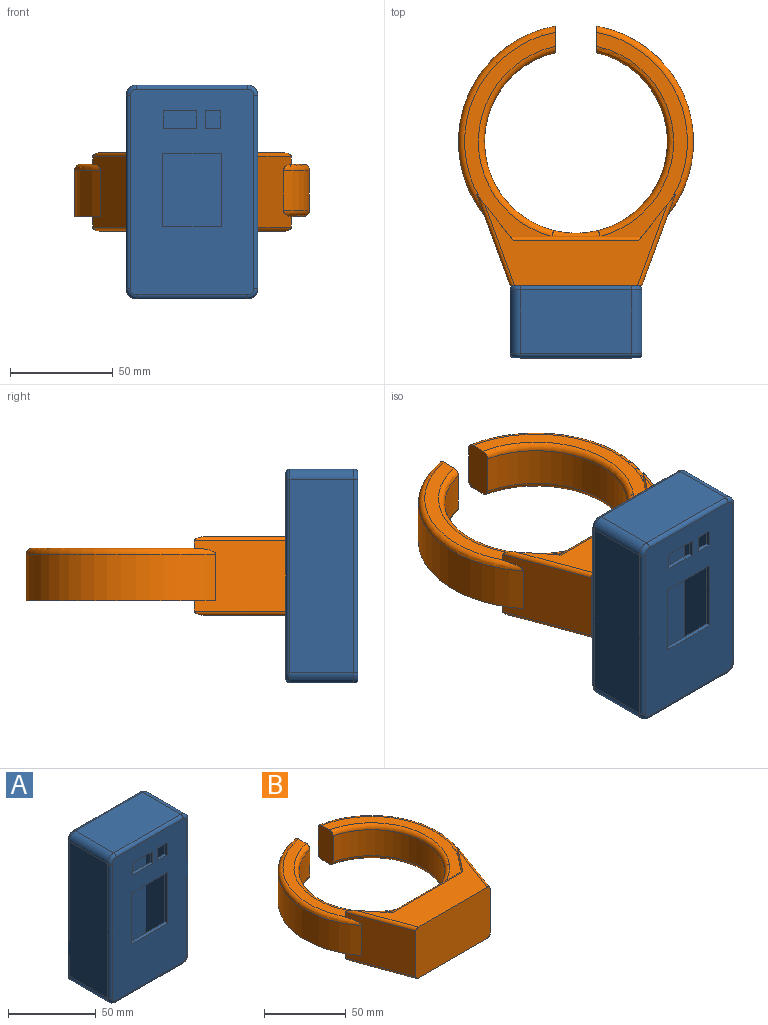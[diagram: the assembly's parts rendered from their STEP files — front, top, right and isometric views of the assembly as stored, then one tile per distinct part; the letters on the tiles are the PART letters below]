
ASSEMBLY  parts=2 mates=1
PART A: 44 faces, bbox 64.8x35x104.8 mm
  f0: plane 100x60mm, normal (0,-1,0), area 4771.6mm2, adj f11,f12,f13,f14,f15,f16,f17,f18
  f1: plane 100x60mm, normal (0,1,0), area 4779.3mm2, adj f27,f28,f29,f30,f31,f32,f33,f34
  f2: plane 54x31mm, normal (0,0,1), area 1674mm2, adj f9,f10,f11,f19
  f3: plane 94x31mm, normal (1,0,0), area 2914mm2, adj f8,f9,f14,f22
  f4: plane 94x31mm, normal (-1,0,0), area 2914mm2, adj f7,f10,f15,f23
  f5: plane 100x60mm, normal (0,1,0), area 5992.3mm2, adj f19,f20,f21,f22,f23,f24,f25,f26
  f6: plane 54x31mm, normal (0,0,-1), area 1674mm2, adj f7,f8,f18,f26
  f7: cylinder r=5mm len=31mm, axis (0,1,0), area 243.5mm2, adj f4,f6,f17,f25
  f8: cylinder r=5mm len=31mm, axis (0,-1,0), area 243.5mm2, adj f3,f6,f16,f24
  f9: cylinder r=5mm len=31mm, axis (0,-1,0), area 243.5mm2, adj f2,f3,f12,f20
  f10: cylinder r=5mm len=31mm, axis (0,1,0), area 243.5mm2, adj f2,f4,f13,f21
  f11: cylinder r=2mm len=54mm, axis (-1,0,0), area 169.6mm2, adj f0,f2,f12,f13
  f12: torus R=3mm, axis (0,-1,0), area 21.1mm2, adj f0,f9,f11,f14
  f13: torus R=3mm, axis (0,-1,0), area 21.1mm2, adj f0,f10,f11,f15
  f14: cylinder r=2mm len=94mm, axis (0,0,1), area 295.3mm2, adj f0,f3,f12,f16
  f15: cylinder r=2mm len=94mm, axis (0,0,-1), area 295.3mm2, adj f0,f4,f13,f17
  f16: torus R=3mm, axis (0,-1,0), area 21.1mm2, adj f0,f8,f14,f18
  f17: torus R=3mm, axis (0,-1,0), area 21.1mm2, adj f0,f7,f15,f18
  f18: cylinder r=2mm len=54mm, axis (-1,0,0), area 169.6mm2, adj f0,f6,f16,f17
  f19: cylinder r=2mm len=54mm, axis (1,0,0), area 169.6mm2, adj f2,f5,f20,f21
  f20: torus R=3mm, axis (0,-1,0), area 21.1mm2, adj f5,f9,f19,f22
  f21: torus R=3mm, axis (0,-1,0), area 21.1mm2, adj f5,f10,f19,f23
  f22: cylinder r=2mm len=94mm, axis (0,0,-1), area 295.3mm2, adj f3,f5,f20,f24
  f23: cylinder r=2mm len=94mm, axis (0,0,1), area 295.3mm2, adj f4,f5,f21,f25
  f24: torus R=3mm, axis (0,-1,0), area 21.1mm2, adj f5,f8,f22,f26
  f25: torus R=3mm, axis (0,-1,0), area 21.1mm2, adj f5,f7,f23,f26
  f26: cylinder r=2mm len=54mm, axis (1,0,0), area 169.6mm2, adj f5,f6,f24,f25
  f27: plane 7.5x2mm, normal (0,0,-1), area 15mm2, adj f0,f1,f28,f30
  f28: plane 8.4x2mm, normal (1,0,0), area 16.8mm2, adj f0,f1,f27,f29
  f29: plane 7.5x2mm, normal (0,0,1), area 15mm2, adj f0,f1,f28,f30
  f30: plane 8.4x2mm, normal (-1,0,0), area 16.8mm2, adj f0,f1,f27,f29
  f31: plane 16.3x2mm, normal (0,0,-1), area 32.6mm2, adj f0,f1,f32,f34
  f32: plane 8.4x2mm, normal (1,0,0), area 16.8mm2, adj f0,f1,f31,f33
  f33: plane 16.3x2mm, normal (0,0,1), area 32.6mm2, adj f0,f1,f32,f34
  f34: plane 8.4x2mm, normal (-1,0,0), area 16.8mm2, adj f0,f1,f31,f33
  f35: plane 60x31mm, normal (0,0,1), area 1860mm2, adj f1,f37,f38,f39
  f36: plane 60x31mm, normal (0,0,-1), area 1860mm2, adj f1,f37,f38,f39
  f37: plane 100x31mm, normal (1,0,0), area 3100mm2, adj f1,f35,f36,f38
  f38: plane 100x60mm, normal (0,-1,0), area 6000mm2, adj f35,f36,f37,f39
  f39: plane 100x31mm, normal (-1,0,0), area 3100mm2, adj f1,f35,f36,f38
  f40: plane 28.65x2mm, normal (0,0,1), area 57.3mm2, adj f0,f1,f41,f43
  f41: plane 35.63x2mm, normal (-1,0,0), area 71.3mm2, adj f0,f1,f40,f42
  f42: plane 28.65x2mm, normal (0,0,-1), area 57.3mm2, adj f0,f1,f41,f43
  f43: plane 35.63x2mm, normal (1,0,0), area 71.3mm2, adj f0,f1,f40,f42
PART B: 38 faces, bbox 124.1x132x38.5 mm
  f0: plane 102.35x47.15mm, normal (0,0,-1), area 1190.9mm2, adj f2,f6,f10,f17,f21,f22,f27
  f1: plane 99.3x44.15mm, normal (0,0,1), area 861.4mm2, adj f13,f15,f16,f20,f29,f32
  f2: cylinder r=57.15mm len=92.09mm, axis (0,0,-1), area 2652.9mm2, adj f0,f17,f22,f24
  f3: plane 99.3x44.15mm, normal (0,0,1), area 861.4mm2, adj f5,f15,f17,f23,f24,f31
  f4: plane 99.3x44.15mm, normal (0,0,-1), area 861.4mm2, adj f7,f10,f16,f18,f25,f28
  f5: plane 4.15x0.08mm, normal (-1,0,0), area 0.3mm2, adj f3,f15,f23,f37
  f6: plane 7.11x0.08mm, normal (-1,0,0), area 0.6mm2, adj f0,f10,f12,f21
  f7: plane 7.11x0.08mm, normal (1,0,0), area 0.6mm2, adj f4,f10,f12,f18
  f8: cylinder r=57.15mm len=92.09mm, axis (0,0,-1), area 2297.6mm2, adj f16,f19,f28,f32
  f9: cylinder r=44.45mm len=88.9mm, axis (0,0,-1), area 5026.8mm2, adj f16,f17,f25,f26,f27,f29,f30,f31
  f10: plane 64.12x7.24mm, normal (0,1,0), area 455.2mm2, adj f0,f4,f6,f7,f12,f26
  f11: plane 88.69x39.49mm, normal (0,0,1), area 1622.1mm2, adj f14,f20,f23,f33,f35,f37
  f12: plane 88.69x39.49mm, normal (0,0,-1), area 1747.2mm2, adj f6,f7,f10,f14,f18,f21,f34,f36
  f13: plane 4.15x0.08mm, normal (1,0,0), area 0.3mm2, adj f1,f15,f20,f37
  f14: plane 64.31x38.41mm, normal (0,-1,0), area 2434.7mm2, adj f11,f12,f19,f22,f33,f34,f35,f36
  f15: plane 64.12x3.71mm, normal (0,1,0), area 229.6mm2, adj f1,f3,f5,f13,f30,f37
  f16: plane 25.66x13.22mm, normal (-1,0,0), area 321.2mm2, adj f1,f4,f8,f9,f25,f28,f29,f32
  f17: plane 25.66x13.22mm, normal (1,0,0), area 323.2mm2, adj f0,f2,f3,f9,f24,f27,f31
  f18: plane 20.61x16.36mm, normal (-0.78,0.62,0), area 183.9mm2, adj f4,f7,f12,f19,f28,f36
  f19: plane 44.48x34.1mm, normal (0.94,-0.34,0), area 1350.8mm2, adj f8,f14,f18,f20,f28,f32,f35,f36
  f20: plane 22.87x18.22mm, normal (-0.78,0.62,0), area 144.9mm2, adj f1,f11,f13,f19,f32,f35,f37
  f21: plane 20.56x16.31mm, normal (0.78,0.62,0), area 183.9mm2, adj f0,f6,f12,f22,f34
  f22: plane 44.48x34.1mm, normal (-0.94,-0.34,0), area 1343.8mm2, adj f0,f2,f14,f21,f23,f24,f33,f34
  f23: plane 22.87x18.22mm, normal (0.78,0.62,0), area 144.9mm2, adj f3,f5,f11,f22,f24,f33,f37
  f24: torus R=54.15mm, axis (0,0,1), area 528.5mm2, adj f2,f3,f17,f22,f23
  f25: torus R=47.45mm, axis (0,0,1), area 573.9mm2, adj f4,f9,f16,f26
  f26: bspline ~25.57x3.41mm, area 83.2mm2, adj f9,f10,f25,f27
  f27: torus R=47.45mm, axis (0,0,1), area 573.9mm2, adj f0,f9,f17,f26
  f28: torus R=54.15mm, axis (0,0,1), area 528.5mm2, adj f4,f8,f16,f18,f19
  f29: torus R=47.45mm, axis (0,0,1), area 573.9mm2, adj f1,f9,f16,f30
  f30: bspline ~25.57x3.41mm, area 83.2mm2, adj f9,f15,f29,f31
  f31: torus R=47.45mm, axis (0,0,1), area 573.9mm2, adj f3,f9,f17,f30
  f32: torus R=54.15mm, axis (0,0,1), area 528.5mm2, adj f1,f8,f16,f19,f20
  f33: cylinder r=2mm len=45.86mm, axis (0.34,-0.94,0), area 143.1mm2, adj f11,f14,f22,f23
  f34: cylinder r=2mm len=45.86mm, axis (-0.34,0.94,0), area 143.1mm2, adj f12,f14,f21,f22
  f35: cylinder r=2mm len=45.86mm, axis (0.34,0.94,0), area 143.1mm2, adj f11,f14,f19,f20
  f36: cylinder r=2mm len=45.86mm, axis (-0.34,-0.94,0), area 143.1mm2, adj f12,f14,f18,f19
  f37: cylinder r=2mm len=64mm, axis (-1,0,0), area 197.1mm2, adj f5,f11,f13,f15,f20,f23
PLACE A t=(4.03,-12.79,8.33)mm
PLACE B t=(4.03,92.21,-4.61)mm
MATE planar B.f14 <-> A.f5  axis (0,-1,0) through (4.03,22.21,7.33)mm
